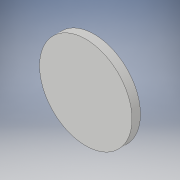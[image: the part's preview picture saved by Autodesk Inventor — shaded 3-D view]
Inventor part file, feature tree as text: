
AUTODESK INVENTOR PART (.ipt)
format: ipt  version: 2019 (Build 230136000, 136)  size: 90,624 bytes
history: native  units: mm
features: other x1, extrude x1, sketch x1
ambient origin geometry x8: Origin, YZ Plane, XZ Plane, XY Plane, X Axis, Y Axis, Z Axis, Center Point
bodies: Body1 (feature_tree)
feature tree (3):
  other  "實體1"
  extrude  "擠出1"  Depth=109.5mm
  sketch  "草圖1"
